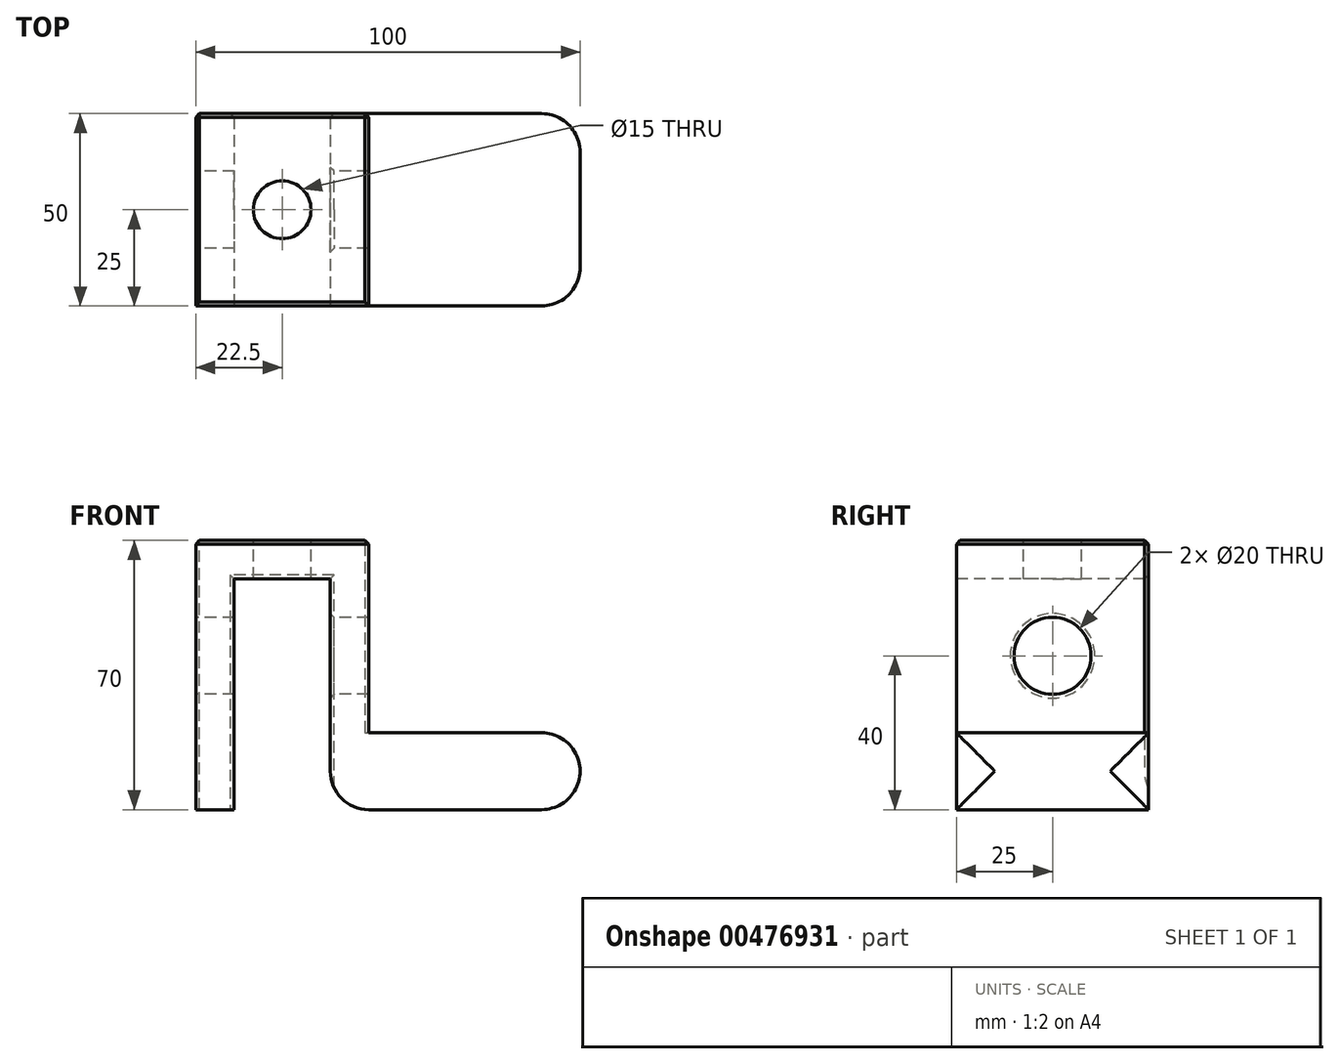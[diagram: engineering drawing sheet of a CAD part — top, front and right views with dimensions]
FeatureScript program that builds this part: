
annotation { "Feature Type Name" : "Feature", "Feature Type Description" : "" }
export const myFeature = defineFeature(function(context is Context, id is Id, definition is map)
    precondition{}
    {
        {
            var Q0;
            Q0=qCreatedBy(makeId("Top.planeOp"),FACE);
            var sketch = newSketch(context, id + "F0", { "sketchPlane" : qUnion([Q0])});
            skLineSegment(sketch, "E0.bottom", {"start": v(0, 0) * mm, "end": v(100, 0) * mm});
            skLineSegment(sketch, "E0.top", {"start": v(0, 50) * mm, "end": v(100, 50) * mm});
            skLineSegment(sketch, "E0.left", {"start": v(0, 0) * mm, "end": v(0, 50) * mm});
            skLineSegment(sketch, "E0.right", {"start": v(100, 0) * mm, "end": v(100, 50) * mm});
            skSolve(sketch);
        }
        {
            var Q0;
            Q0=makeQuery(id+"F0.imprint","IMPRINT",FACE,{"disambiguationData":[TD([[makeQuery(id+"F0.imprint","IMPRINT",EDGE,{"derivedFrom":sQuery(id+"F0.wireOp",EDGE,"E0.bottom")}),1.0]])]});
            extrude(context, id + "F1", {"entities" : qUnion([Q0]), "depth" : 20 * mm});
        }
        {
            var Q0;
            Q0=makeQuery(id+"F1.opExtrude","CAP_FACE",FACE,{"disambiguationData":[OSD([sQuery(id+"F0.wireOp",EDGE,"E0.bottom"),sQuery(id+"F0.wireOp",EDGE,"E0.top"),sQuery(id+"F0.wireOp",EDGE,"E0.left"),sQuery(id+"F0.wireOp",EDGE,"E0.right")])],"isStart":false});
            var sketch = newSketch(context, id + "F2", { "sketchPlane" : qUnion([Q0])});
            skLineSegment(sketch, "E1.bottom", {"start": v(0, 0) * mm, "end": v(45, 0) * mm});
            skLineSegment(sketch, "E1.top", {"start": v(0, 50) * mm, "end": v(45, 50) * mm});
            skLineSegment(sketch, "E1.left", {"start": v(0, 0) * mm, "end": v(0, 50) * mm});
            skLineSegment(sketch, "E1.right", {"start": v(45, 0) * mm, "end": v(45, 50) * mm});
            skSolve(sketch);
        }
        {
            var Q0;
            Q0 = qSketchRegion(id + "F2", true);
            extrude(context, id + "F3", {"entities" : qUnion([Q0]), "operationType" : NewBodyOperationType.ADD, "depth" : 50 * mm});
        }
        {
            var Q0;
            Q0=makeQuery(id+"F3.boolean.opBoolean","MERGE",FACE,{"derivedFrom":[makeQuery(id+"F1.opExtrude","SWEPT_FACE",FACE,{"disambiguationData":[OSD([sQuery(id+"F0.wireOp",EDGE,"E0.bottom")])]}),makeQuery(id+"F3.opExtrude","SWEPT_FACE",FACE,{"disambiguationData":[OSD([sQuery(id+"F2.wireOp",EDGE,"E1.bottom")])]})]});
            var sketch = newSketch(context, id + "F4", { "sketchPlane" : qUnion([Q0])});
            skLineSegment(sketch, "E2.bottom", {"start": v(10, 0) * mm, "end": v(35, 0) * mm});
            skLineSegment(sketch, "E2.top", {"start": v(10, 60) * mm, "end": v(35, 60) * mm});
            skLineSegment(sketch, "E2.left", {"start": v(10, 0) * mm, "end": v(10, 60) * mm});
            skLineSegment(sketch, "E2.right", {"start": v(35, 0) * mm, "end": v(35, 60) * mm});
            skSolve(sketch);
        }
        {
            var Q0;
            Q0 = qSketchRegion(id + "F4", true);
            extrude(context, id + "F5", {"entities" : qUnion([Q0]), "operationType" : NewBodyOperationType.REMOVE, "endBound" : BoundingType.THROUGH_ALL, "oppositeDirection" : true, "depth" : 25 * mm});
        }
        {
            var Q0;
            Q0=makeQuery(id+"F3.boolean.opBoolean","MERGE",FACE,{"derivedFrom":[makeQuery(id+"F1.opExtrude","SWEPT_FACE",FACE,{"disambiguationData":[OSD([sQuery(id+"F0.wireOp",EDGE,"E0.left")])]}),makeQuery(id+"F3.opExtrude","SWEPT_FACE",FACE,{"disambiguationData":[OSD([sQuery(id+"F2.wireOp",EDGE,"E1.left")])]})]});
            var sketch = newSketch(context, id + "F6", { "sketchPlane" : qUnion([Q0])});
            skCircle(sketch, "E3", {"center": v(-25, 40) * mm, "radius": 10 * mm});
            skSolve(sketch);
        }
        {
            var Q0;
            Q0 = qSketchRegion(id + "F6", true);
            var Q1;
            Q1=makeQuery(id+"F3.opExtrude","SWEPT_FACE",FACE,{"disambiguationData":[OSD([sQuery(id+"F2.wireOp",EDGE,"E1.right")])]});
            extrude(context, id + "F7", {"entities" : qUnion([Q0]), "operationType" : NewBodyOperationType.REMOVE, "endBound" : BoundingType.UP_TO_SURFACE, "oppositeDirection" : true, "endBoundEntityFace" : qUnion([Q1]), "depth" : 25 * mm});
        }
        {
            var Q0;
            Q0=makeQuery(id+"F3.opExtrude","CAP_FACE",FACE,{"disambiguationData":[OSD([sQuery(id+"F2.wireOp",EDGE,"E1.bottom"),sQuery(id+"F2.wireOp",EDGE,"E1.top"),sQuery(id+"F2.wireOp",EDGE,"E1.left"),sQuery(id+"F2.wireOp",EDGE,"E1.right")])],"isStart":false});
            var sketch = newSketch(context, id + "F8", { "sketchPlane" : qUnion([Q0])});
            skLineSegment(sketch, "E4", {"start": v(0, 0) * mm, "end": v(45, 50) * mm, "construction": true});
            skLineSegment(sketch, "E5", {"start": v(0, 50) * mm, "end": v(45, 0) * mm, "construction": true});
            skCircle(sketch, "E6", {"center": v(22.5, 25) * mm, "radius": 7.5 * mm});
            skSolve(sketch);
        }
        {
            var Q0;
            Q0 = qSketchRegion(id + "F8", true);
            extrude(context, id + "F9", {"entities" : qUnion([Q0]), "operationType" : NewBodyOperationType.REMOVE, "endBound" : BoundingType.THROUGH_ALL, "oppositeDirection" : true, "depth" : 25 * mm});
        }
        {
            var Q0;
            Q0=makeQuery(id+"F3.opExtrude","SWEPT_EDGE",EDGE,{"disambiguationData":[OSD([sQuery(id+"F0.wireOp",EDGE,"E0.top"),sQuery(id+"F2.wireOp",EDGE,"E1.top"),sQuery(id+"F2.wireOp",EDGE,"E1.right")])]});
            var Q1;
            Q1=makeQuery(id+"F3.opExtrude","CAP_EDGE",EDGE,{"disambiguationData":[OSD([sQuery(id+"F2.wireOp",EDGE,"E1.top")])],"isStart":false});
            var Q2;
            Q2=makeQuery(id+"F3.opExtrude","CAP_EDGE",EDGE,{"disambiguationData":[OSD([sQuery(id+"F2.wireOp",EDGE,"E1.right")])],"isStart":false});
            var Q3;
            Q3=makeQuery(id+"F3.opExtrude","CAP_EDGE",EDGE,{"disambiguationData":[OSD([sQuery(id+"F2.wireOp",EDGE,"E1.left")])],"isStart":false});
            var Q4;
            Q4=makeQuery(id+"F3.boolean.opBoolean","MERGE",EDGE,{"derivedFrom":[makeQuery(id+"F1.opExtrude","SWEPT_EDGE",EDGE,{"disambiguationData":[OSD([sQuery(id+"F0.wireOp",EDGE,"E0.top"),sQuery(id+"F0.wireOp",EDGE,"E0.left")])]}),makeQuery(id+"F3.opExtrude","SWEPT_EDGE",EDGE,{"disambiguationData":[OSD([sQuery(id+"F2.wireOp",EDGE,"E1.top"),sQuery(id+"F2.wireOp",EDGE,"E1.left")])]})]});
            var Q5;
            Q5=makeQuery(id+"F5.boolean.opBoolean","INTERSECT",EDGE,{"derivedFrom":[makeQuery(id+"F3.boolean.opBoolean","MERGE",FACE,{"derivedFrom":[makeQuery(id+"F1.opExtrude","SWEPT_FACE",FACE,{"disambiguationData":[OSD([sQuery(id+"F0.wireOp",EDGE,"E0.top")])]}),makeQuery(id+"F3.opExtrude","SWEPT_FACE",FACE,{"disambiguationData":[OSD([sQuery(id+"F2.wireOp",EDGE,"E1.top")])]})]}),makeQuery(id+"F5.opExtrude","SWEPT_FACE",FACE,{"disambiguationData":[OSD([sQuery(id+"F4.wireOp",EDGE,"E2.left")])]})]});
            var Q6;
            Q6=makeQuery(id+"F5.boolean.opBoolean","INTERSECT",EDGE,{"derivedFrom":[makeQuery(id+"F3.boolean.opBoolean","MERGE",FACE,{"derivedFrom":[makeQuery(id+"F1.opExtrude","SWEPT_FACE",FACE,{"disambiguationData":[OSD([sQuery(id+"F0.wireOp",EDGE,"E0.top")])]}),makeQuery(id+"F3.opExtrude","SWEPT_FACE",FACE,{"disambiguationData":[OSD([sQuery(id+"F2.wireOp",EDGE,"E1.top")])]})]}),makeQuery(id+"F5.opExtrude","SWEPT_FACE",FACE,{"disambiguationData":[OSD([sQuery(id+"F4.wireOp",EDGE,"E2.top")])]})]});
            var Q7;
            Q7=makeQuery(id+"F5.boolean.opBoolean","INTERSECT",EDGE,{"derivedFrom":[makeQuery(id+"F3.boolean.opBoolean","MERGE",FACE,{"derivedFrom":[makeQuery(id+"F1.opExtrude","SWEPT_FACE",FACE,{"disambiguationData":[OSD([sQuery(id+"F0.wireOp",EDGE,"E0.top")])]}),makeQuery(id+"F3.opExtrude","SWEPT_FACE",FACE,{"disambiguationData":[OSD([sQuery(id+"F2.wireOp",EDGE,"E1.top")])]})]}),makeQuery(id+"F5.opExtrude","SWEPT_FACE",FACE,{"disambiguationData":[OSD([sQuery(id+"F4.wireOp",EDGE,"E2.right")])]})]});
            var Q8;
            Q8=makeQuery(id+"F7.boolean.opBoolean","INTERSECT",EDGE,{"derivedFrom":[makeQuery(id+"F5.boolean.opBoolean","COPY",FACE,{"derivedFrom":makeQuery(id+"F5.opExtrude","SWEPT_FACE",FACE,{"disambiguationData":[OSD([sQuery(id+"F4.wireOp",EDGE,"E2.right")])]})}),makeQuery(id+"F7.opExtrude","SWEPT_FACE",FACE,{"disambiguationData":[OSD([sQuery(id+"F6.wireOp",EDGE,"E3")])]})]});
            var Q9;
            Q9=makeQuery(id+"F9.boolean.opBoolean","COPY",EDGE,{"derivedFrom":makeQuery(id+"F9.opExtrude","CAP_EDGE",EDGE,{"disambiguationData":[OSD([sQuery(id+"F8.wireOp",EDGE,"E6")])],"isStart":true})});
            var Q10;
            Q10=makeQuery(id+"F3.opExtrude","CAP_EDGE",EDGE,{"disambiguationData":[OSD([sQuery(id+"F2.wireOp",EDGE,"E1.bottom")])],"isStart":false});
            chamfer(context, id + "F10", {"entities" : qUnion([Q0, Q1, Q2, Q3, Q4, Q5, Q6, Q7, Q8, Q9, Q10]), "width" : 1 * mm, "tangentPropagation" : true});
        }
        {
            var Q0;
            Q0=makeQuery(id+"F5.boolean.opBoolean","COPY",EDGE,{"derivedFrom":makeQuery(id+"F5.opExtrude","SWEPT_EDGE",EDGE,{"disambiguationData":[OSD([sQuery(id+"F0.wireOp",EDGE,"E0.bottom"),sQuery(id+"F4.wireOp",EDGE,"E2.bottom"),sQuery(id+"F4.wireOp",EDGE,"E2.right")])]})});
            var Q1;
            Q1=makeQuery(id+"F1.opExtrude","CAP_EDGE",EDGE,{"disambiguationData":[OSD([sQuery(id+"F0.wireOp",EDGE,"E0.right")])],"isStart":true});
            var Q2;
            Q2=makeQuery(id+"F1.opExtrude","SWEPT_EDGE",EDGE,{"disambiguationData":[OSD([sQuery(id+"F0.wireOp",EDGE,"E0.bottom"),sQuery(id+"F0.wireOp",EDGE,"E0.right")])]});
            var Q3;
            Q3=makeQuery(id+"F1.opExtrude","CAP_EDGE",EDGE,{"disambiguationData":[OSD([sQuery(id+"F0.wireOp",EDGE,"E0.right")])],"isStart":false});
            var Q4;
            Q4=makeQuery(id+"F1.opExtrude","SWEPT_EDGE",EDGE,{"disambiguationData":[OSD([sQuery(id+"F0.wireOp",EDGE,"E0.top"),sQuery(id+"F0.wireOp",EDGE,"E0.right")])]});
            fillet(context, id + "F11", {"entities" : qUnion([Q0, Q1, Q2, Q3, Q4]), "radius" : 10 * mm, "tangentPropagation" : true, "allowEdgeOverflow" : false});
        }
    });
